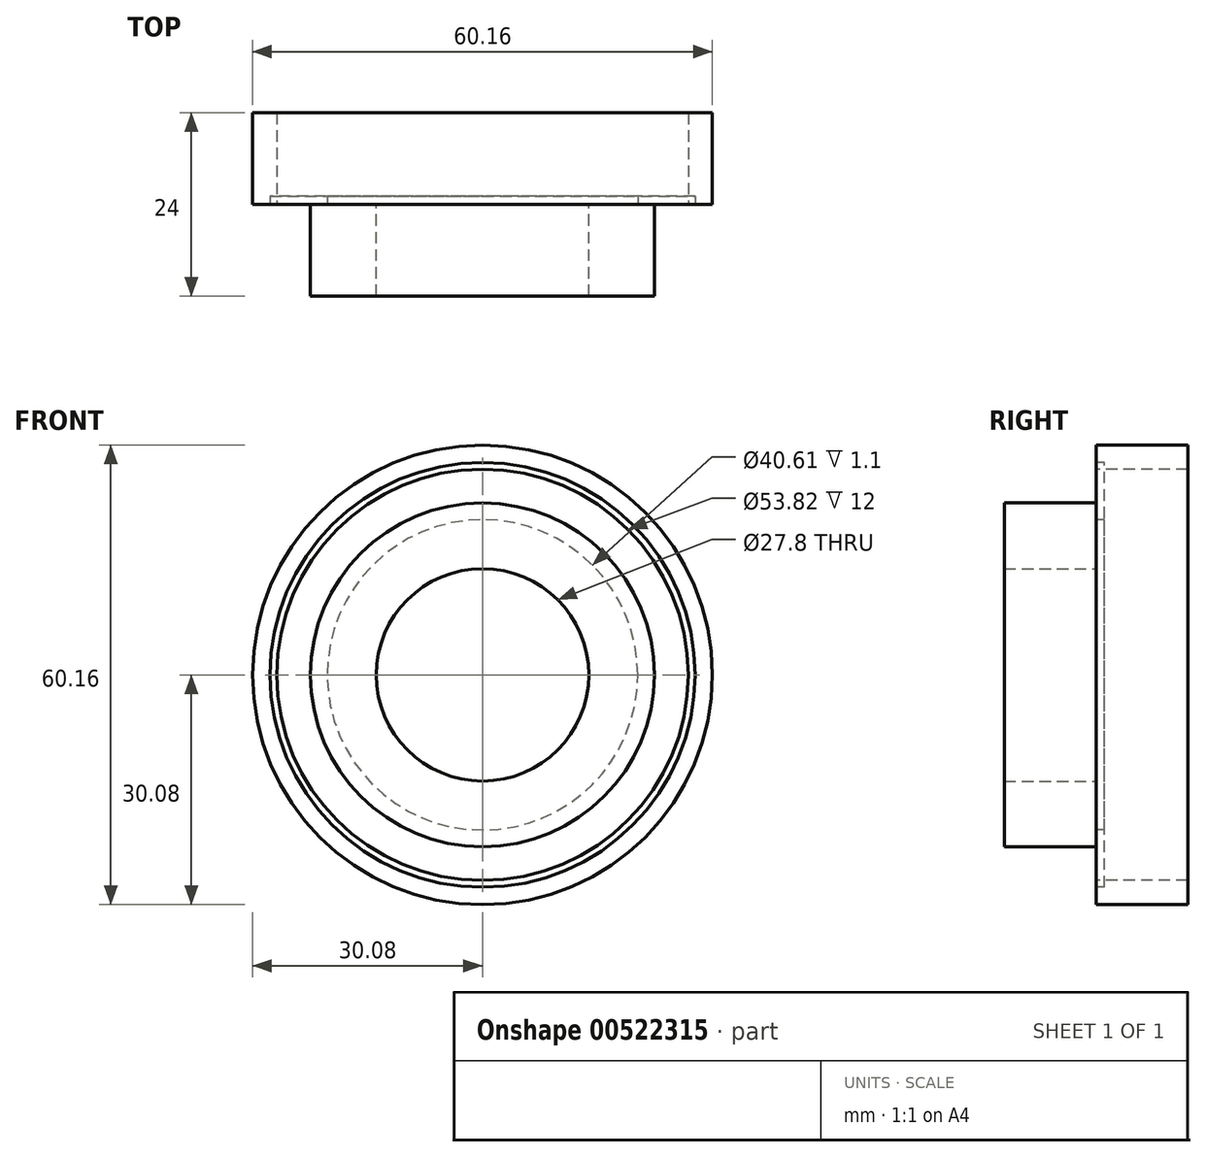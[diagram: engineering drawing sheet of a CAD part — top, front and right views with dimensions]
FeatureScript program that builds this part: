
annotation { "Feature Type Name" : "Feature", "Feature Type Description" : "" }
export const myFeature = defineFeature(function(context is Context, id is Id, definition is map)
    precondition{}
    {
        {
            var Q0;
            Q0=qCreatedBy(makeId("Front.planeOp"),FACE);
            var sketch = newSketch(context, id + "F0", { "sketchPlane" : qUnion([Q0])});
            skCircle(sketch, "E0", {"center": v(0, 0) * mm, "radius": 22.5 * mm});
            skCircle(sketch, "E1", {"center": v(0, 0) * mm, "radius": 13.9 * mm});
            skSolve(sketch);
        }
        {
            var Q0;
            Q0 = qSketchRegion(id + "F0", true);
            extrude(context, id + "F1", {"entities" : qUnion([Q0]), "depth" : 12 * mm, "offsetDistance" : 25 * mm});
        }
        {
            var Q0;
            Q0=qCreatedBy(makeId("Front.planeOp"),FACE);
            var sketch = newSketch(context, id + "F2", { "sketchPlane" : qUnion([Q0])});
            skCircle(sketch, "E2", {"center": v(0, 0) * mm, "radius": 30.07 * mm});
            skCircle(sketch, "E3", {"center": v(0, 0) * mm, "radius": 26.91 * mm});
            skSolve(sketch);
        }
        {
            var Q0;
            Q0 = qSketchRegion(id + "F2", true);
            extrude(context, id + "F3", {"entities" : qUnion([Q0]), "oppositeDirection" : true, "depth" : 12 * mm, "offsetDistance" : 25 * mm});
        }
        {
            var Q0;
            Q0=qCreatedBy(makeId("Front.planeOp"),FACE);
            var sketch = newSketch(context, id + "F4", { "sketchPlane" : qUnion([Q0])});
            skCircle(sketch, "E4", {"center": v(0, 0) * mm, "radius": 20.3 * mm});
            skCircle(sketch, "E5", {"center": v(0, 0) * mm, "radius": 27.8 * mm});
            skSolve(sketch);
        }
        {
            var Q0;
            Q0=makeQuery(id+"F4.imprint","IMPRINT",FACE,{"disambiguationData":[TD([[makeQuery(id+"F4.imprint","IMPRINT",EDGE,{"derivedFrom":sQuery(id+"F4.wireOp",EDGE,"E4")}),-1.0]])]});
            var Q1;
            Q1=sQuery(id+"F4.wireOp",EDGE,"E5");
            var Q2;
            Q2=sQuery(id+"F4.wireOp",EDGE,"E4");
            extrude(context, id + "F5", {"entities" : qUnion([Q0]), "surfaceEntities" : qUnion([Q1, Q2]), "oppositeDirection" : true, "depth" : 1.1 * mm, "offsetDistance" : 25 * mm});
        }
    });
